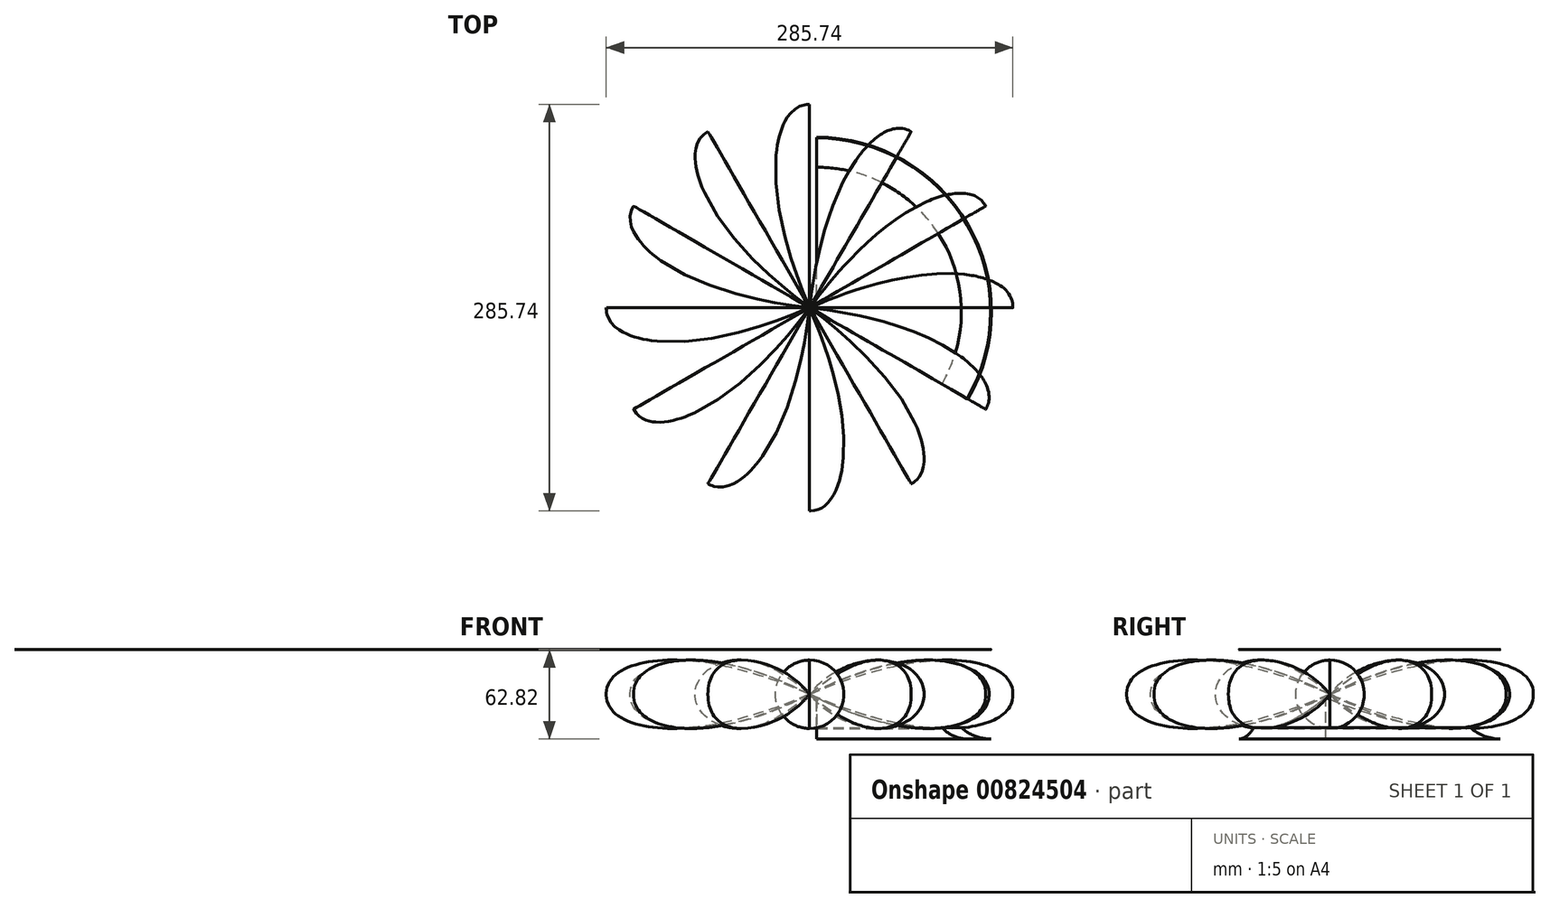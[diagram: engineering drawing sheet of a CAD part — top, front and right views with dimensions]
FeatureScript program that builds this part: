
annotation { "Feature Type Name" : "Feature", "Feature Type Description" : "" }
export const myFeature = defineFeature(function(context is Context, id is Id, definition is map)
    precondition{}
    {
        {
            var Q0;
            Q0=qCreatedBy(makeId("Top.planeOp"),FACE);
            var sketch = newSketch(context, id + "F0", { "sketchPlane" : qUnion([Q0])});
            skFitSpline(sketch, "E0", {"points": [v(-86.94, 0) * mm, v(20.51, 23.51) * mm, v(55.6, 0) * mm], "startDerivative": vector(168, 74.59) * mm, "endDerivative": vector(-3.08, -109.62) * mm});
            skLineSegment(sketch, "E1", {"start": v(-86.94, 0) * mm, "end": v(55.6, 0) * mm});
            skSolve(sketch);
        }
        {
            var Q0;
            Q0=makeQuery(id+"F0.imprint","IMPRINT",FACE,{"disambiguationData":[TD([[makeQuery(id+"F0.imprint","IMPRINT",EDGE,{"derivedFrom":sQuery(id+"F0.wireOp",EDGE,"E0")}),-1.0]])]});
            var Q1;
            Q1=sQuery(id+"F0.wireOp",EDGE,"E1");
            revolve(context, id + "F1", {"surfaceOperationType" : NewSurfaceOperationType.NEW, "entities" : qUnion([Q0]), "axis" : qUnion([Q1]), "revolveType" : RevolveType.SYMMETRIC, "angle" : 180 * degree});
        }
        {
            var Q0;
            Q0=qCreatedBy(makeId("Front.planeOp"),FACE);
            var sketch = newSketch(context, id + "F2", { "sketchPlane" : qUnion([Q0])});
            skLineSegment(sketch, "E2", {"start": v(-87.25, 0) * mm, "end": v(-87.25, 59.9) * mm, "construction": true});
            skSolve(sketch);
        }
        {
            var Q0;
            Q0=makeQuery(id+"F1.opRevolve","SWEPT_BODY",BODY,{"disambiguationData":[OSD([sQuery(id+"F0.wireOp",EDGE,"E0"),sQuery(id+"F0.wireOp",EDGE,"E1")])]});
            var Q1;
            Q1=sQuery(id+"F2.wireOp",EDGE,"E2");
            circularPattern(context, id + "F3", {"entities" : qUnion([Q0]), "axis" : qUnion([Q1]), "angle" : 360 * degree, "instanceCount" : 12, "equalSpace" : true});
        }
        {
            var Q0;
            Q0=makeQuery(id+"F3.opPattern","COPY",FACE,{"derivedFrom":makeQuery(id+"F1.opRevolve","CAP_FACE",FACE,{"disambiguationData":[OSD([sQuery(id+"F0.wireOp",EDGE,"E0"),sQuery(id+"F0.wireOp",EDGE,"E1")])],"isStart":true}),"instanceName":"11"});
            var sketch = newSketch(context, id + "F4", { "sketchPlane" : qUnion([Q0])});
            skCircle(sketch, "E3", {"center": v(52.66, 0) * mm, "radius": 31.41 * mm});
            skLineSegment(sketch, "E4", {"start": v(52.95, 31.41) * mm, "end": v(-69.78, 31.41) * mm});
            skLineSegment(sketch, "E5", {"start": v(52.66, -31.41) * mm, "end": v(-69.78, -31.41) * mm});
            skLineSegment(sketch, "E6", {"start": v(-69.78, -31.41) * mm, "end": v(-69.78, 31.41) * mm});
            skSolve(sketch);
        }
        {
            var Q0;
            {var subQ0=sQuery(id+"F4.wireOp",EDGE,"E4");var subQ1=sQuery(id+"F4.wireOp",EDGE,"E3");var subQ2=makeQuery(id+"F4.imprint","INTERSECT",VERTEX,{"disambiguationData":[OD(1.0)],"derivedFrom":[subQ1,subQ0]});Q0=makeQuery(id+"F4.imprint","IMPRINT",FACE,{"disambiguationData":[TD([[makeQuery(id+"F4.imprint","IMPRINT",EDGE,{"disambiguationData":[TD([[subQ2,-1.0]])],"derivedFrom":subQ1}),-1.0]])]});}
            var Q1;
            {var subQ0=sQuery(id+"F4.wireOp",EDGE,"E4");var subQ1=sQuery(id+"F4.wireOp",EDGE,"E3");var subQ3=makeQuery(id+"F4.imprint","INTERSECT",VERTEX,{"disambiguationData":[OD(1.0)],"derivedFrom":[subQ1,subQ0]});Q1=makeQuery(id+"F4.imprint","IMPRINT",FACE,{"disambiguationData":[TD([[makeQuery(id+"F4.imprint","IMPRINT",EDGE,{"disambiguationData":[TD([[subQ3,-1.0]])],"derivedFrom":subQ1}),1.0]])]});}
            var Q2;
            {var subQ0=sQuery(id+"F4.wireOp",EDGE,"E5");Q2=makeQuery(id+"F4.imprint","IMPRINT",FACE,{"disambiguationData":[TD([[makeQuery(id+"F4.imprint","IMPRINT",EDGE,{"derivedFrom":subQ0}),-1.0]])]});}
            var Q3;
            Q3=sQuery(id+"F4.wireOp",EDGE,"E6");
            revolve(context, id + "F5", {"surfaceOperationType" : NewSurfaceOperationType.NEW, "entities" : qUnion([Q0, Q1, Q2]), "axis" : qUnion([Q3]), "revolveType" : RevolveType.ONE_DIRECTION, "angle" : 120 * degree});
        }
    });
